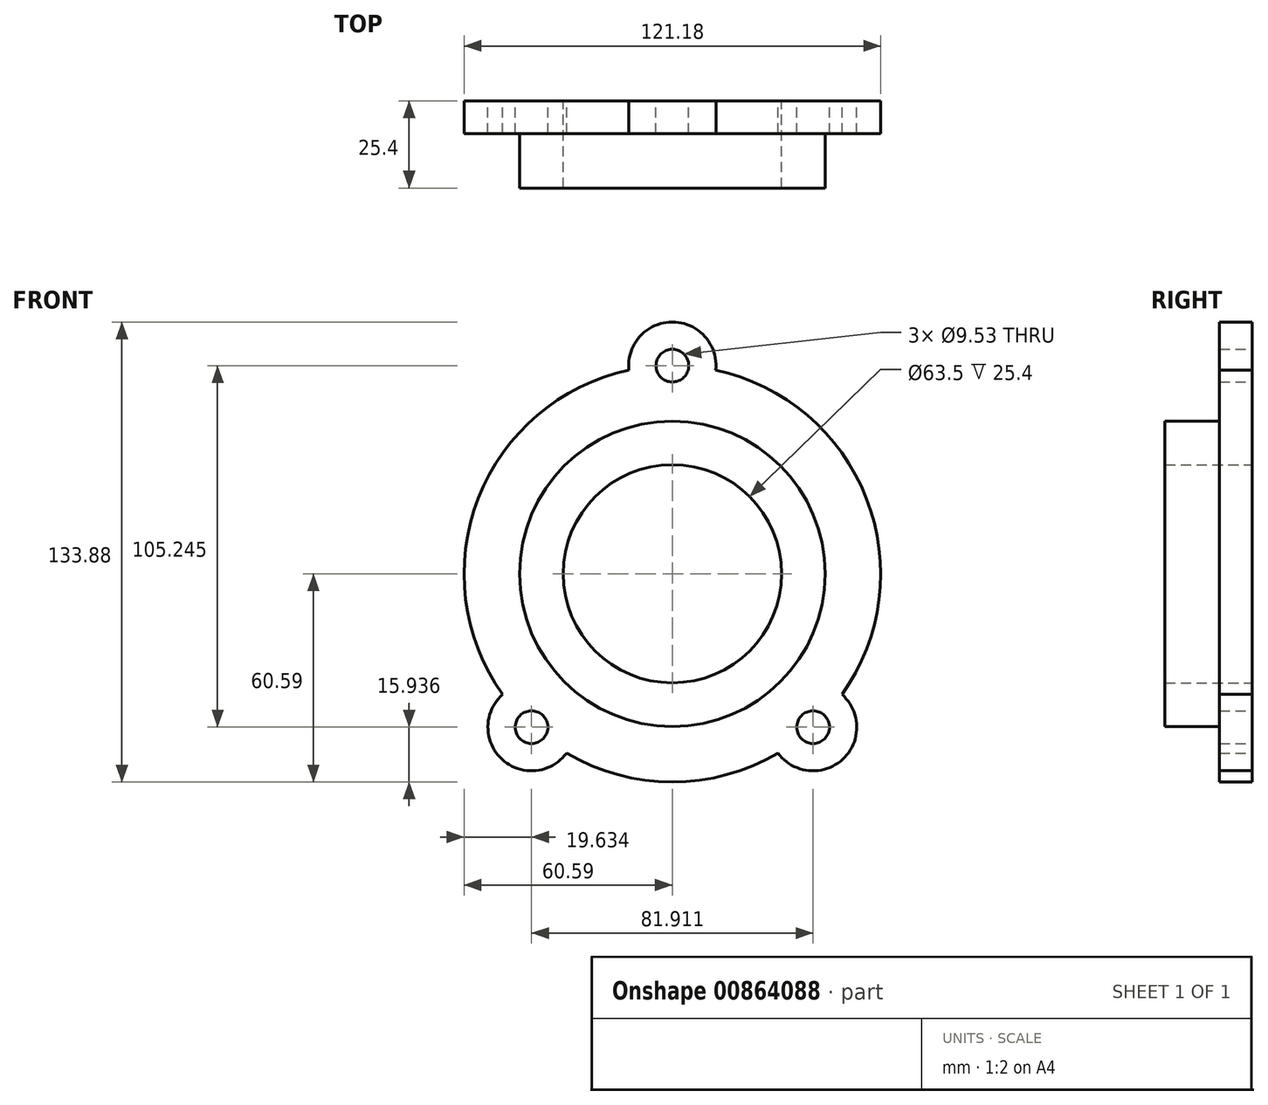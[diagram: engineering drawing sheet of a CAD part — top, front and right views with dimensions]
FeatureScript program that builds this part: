
annotation { "Feature Type Name" : "Feature", "Feature Type Description" : "" }
export const myFeature = defineFeature(function(context is Context, id is Id, definition is map)
    precondition{}
    {
        {
            var Q0;
            Q0=qCreatedBy(makeId("Front.planeOp"),FACE);
            var sketch = newSketch(context, id + "F0", { "sketchPlane" : qUnion([Q0])});
            skCircle(sketch, "E0", {"center": v(0, 0) * mm, "radius": 44.45 * mm});
            skArc(sketch, "E1", {"start": v(49.36, -35.14) * mm, "mid": v(56.47, 21.97) * mm, "end": v(12.63, 59.26) * mm});
            skArc(sketch, "E2", {"start": v(12.63, 59.26) * mm, "mid": v(0, 73.3) * mm, "end": v(-12.63, 59.26) * mm});
            skArc(sketch, "E3", {"start": v(-49.36, -35.14) * mm, "mid": v(-49.54, -54.01) * mm, "end": v(-30.75, -52.2) * mm});
            skArc(sketch, "E4.MirrorC", {"start": v(49.36, -35.14) * mm, "mid": v(49.54, -54.01) * mm, "end": v(30.75, -52.2) * mm});
            skArc(sketch, "E5.trimOffspring", {"start": v(-30.75, -52.2) * mm, "mid": v(0, -60.6) * mm, "end": v(30.75, -52.2) * mm});
            skArc(sketch, "E6.trimOffspring", {"start": v(-12.63, 59.26) * mm, "mid": v(-56.47, 21.97) * mm, "end": v(-49.36, -35.14) * mm});
            skCircle(sketch, "E7", {"center": v(0, 60.6) * mm, "radius": 4.76 * mm});
            skCircle(sketch, "E8", {"center": v(40.96, -44.65) * mm, "radius": 4.76 * mm});
            skCircle(sketch, "E9", {"center": v(-40.96, -44.65) * mm, "radius": 4.76 * mm});
            skCircle(sketch, "E10", {"center": v(0, 0) * mm, "radius": 31.75 * mm});
            skCircle(sketch, "E11", {"center": v(0, 0) * mm, "radius": 19.05 * mm});
            skSolve(sketch);
        }
        {
            var Q0;
            Q0=makeQuery(id+"F0.imprint","IMPRINT",FACE,{"disambiguationData":[TD([[makeQuery(id+"F0.imprint","IMPRINT",EDGE,{"derivedFrom":sQuery(id+"F0.wireOp",EDGE,"E0")}),1.0]])]});
            extrude(context, id + "F1", {"entities" : qUnion([Q0]), "depth" : 25.4 * mm, "offsetDistance" : 25.4 * mm});
        }
        {
            var Q0;
            Q0=makeQuery(id+"F0.imprint","IMPRINT",FACE,{"disambiguationData":[TD([[makeQuery(id+"F0.imprint","IMPRINT",EDGE,{"derivedFrom":sQuery(id+"F0.wireOp",EDGE,"E0")}),-1.0]])]});
            extrude(context, id + "F2", {"entities" : qUnion([Q0]), "operationType" : NewBodyOperationType.ADD, "depth" : 9.52 * mm, "offsetDistance" : 25.4 * mm});
        }
    });
